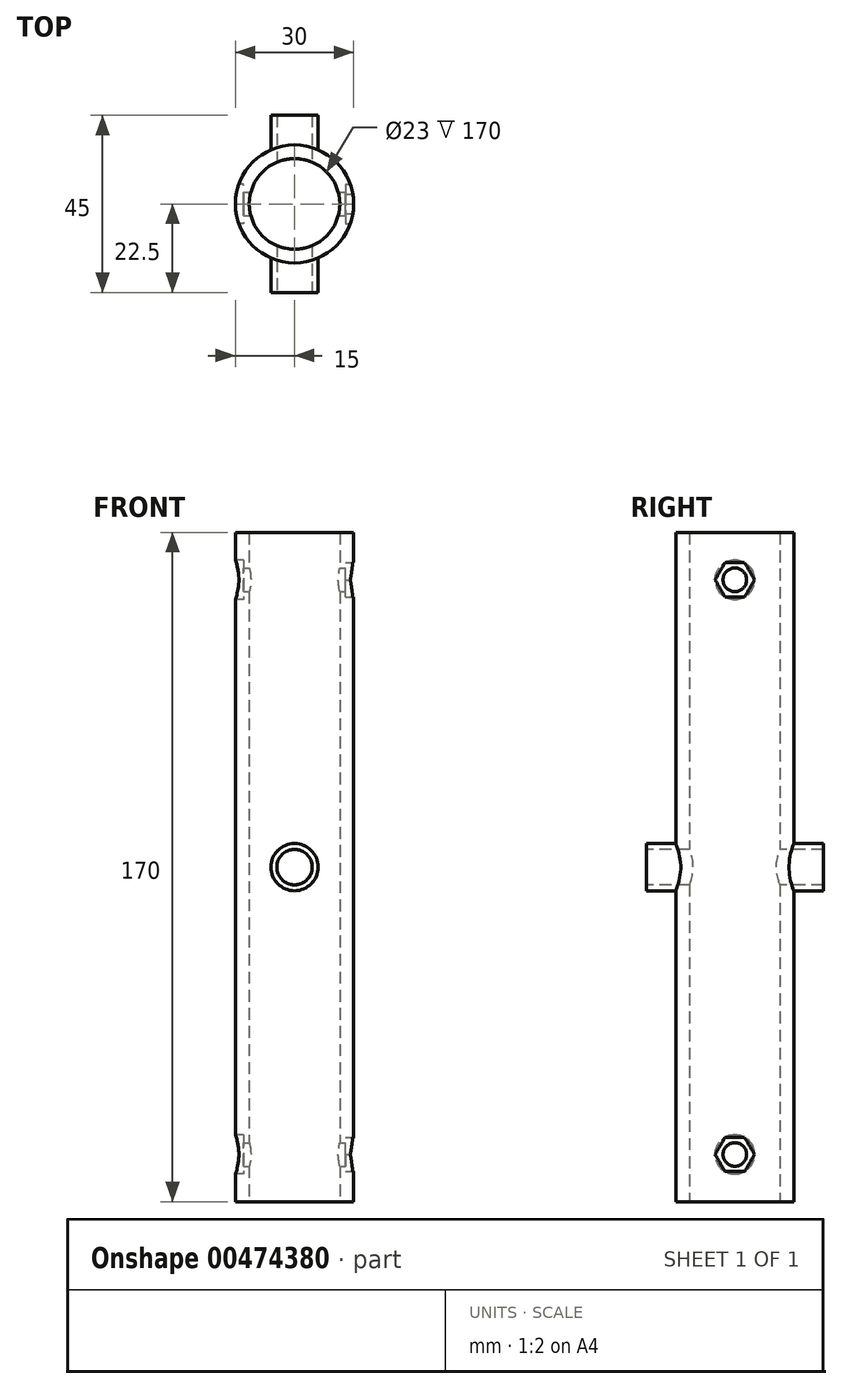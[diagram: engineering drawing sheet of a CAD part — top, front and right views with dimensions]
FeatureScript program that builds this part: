
annotation { "Feature Type Name" : "Feature", "Feature Type Description" : "" }
export const myFeature = defineFeature(function(context is Context, id is Id, definition is map)
    precondition{}
    {
        {
            var Q0;
            Q0=qCreatedBy(makeId("Top.planeOp"),FACE);
            var sketch = newSketch(context, id + "F0", { "sketchPlane" : qUnion([Q0])});
            skCircle(sketch, "E0", {"center": v(0, 0) * mm, "radius": 15 * mm});
            skCircle(sketch, "E1", {"center": v(0, 0) * mm, "radius": 11.5 * mm});
            skSolve(sketch);
        }
        {
            var Q0;
            Q0=makeQuery(id+"F0.imprint","IMPRINT",FACE,{"disambiguationData":[TD([[makeQuery(id+"F0.imprint","IMPRINT",EDGE,{"derivedFrom":sQuery(id+"F0.wireOp",EDGE,"E0")}),1.0]])]});
            extrude(context, id + "F1", {"entities" : qUnion([Q0]), "depth" : 170 * mm});
        }
        {
            var Q0;
            Q0=qCreatedBy(makeId("Front.planeOp"),FACE);
            var sketch = newSketch(context, id + "F2", { "sketchPlane" : qUnion([Q0])});
            skCircle(sketch, "E2", {"center": v(0, 85) * mm, "radius": 4.5 * mm});
            skSolve(sketch);
        }
        {
            var Q0;
            Q0 = qSketchRegion(id + "F2", true);
            extrude(context, id + "F3", {"entities" : qUnion([Q0]), "operationType" : NewBodyOperationType.REMOVE, "endBound" : BoundingType.THROUGH_ALL, "oppositeDirection" : true, "depth" : 25 * mm, "hasSecondDirection" : true, "secondDirectionBound" : SecondDirectionBoundingType.THROUGH_ALL, "secondDirectionOppositeDirection" : false, "secondDirectionDepth" : 25 * mm});
        }
        {
            var Q0;
            Q0=qCreatedBy(makeId("Front.planeOp"),FACE);
            cPlane(context, id + "F4", {"entities" : qUnion([Q0]), "cplaneType" : CPlaneType.OFFSET, "offset" : 17.5 * mm, "width" : 150 * mm, "height" : 150 * mm});
        }
        {
            var Q0;
            Q0=qCreatedBy(id+"F4.planeOp",FACE);
            var sketch = newSketch(context, id + "F5", { "sketchPlane" : qUnion([Q0])});
            skCircle(sketch, "E3", {"center": v(0, 85) * mm, "radius": 6 * mm});
            skCircle(sketch, "E4.0", {"center": v(0, 85) * mm, "radius": 4.5 * mm});
            skSolve(sketch);
        }
        {
            var Q0;
            Q0 = qSketchRegion(id + "F5", true);
            var Q1;
            Q1=makeQuery(id+"F1.opExtrude","SWEPT_FACE",FACE,{"disambiguationData":[OSD([sQuery(id+"F0.wireOp",EDGE,"E0")])]});
            extrude(context, id + "F6", {"entities" : qUnion([Q0]), "operationType" : NewBodyOperationType.ADD, "depth" : 5 * mm, "hasSecondDirection" : true, "secondDirectionBound" : SecondDirectionBoundingType.UP_TO_SURFACE, "secondDirectionOppositeDirection" : true, "secondDirectionBoundEntityFace" : qUnion([Q1]), "secondDirectionDepth" : 25 * mm});
        }
        {
            var Q0;
            Q0=qCreatedBy(makeId("Front.planeOp"),FACE);
            cPlane(context, id + "F7", {"entities" : qUnion([Q0]), "cplaneType" : CPlaneType.OFFSET, "offset" : 17.5 * mm, "oppositeDirection" : true, "width" : 150 * mm, "height" : 150 * mm});
        }
        {
            var Q0;
            Q0=qCreatedBy(id+"F7.planeOp",FACE);
            var sketch = newSketch(context, id + "F8", { "sketchPlane" : qUnion([Q0])});
            skCircle(sketch, "E5.0", {"center": v(0, 85) * mm, "radius": 6 * mm});
            skCircle(sketch, "E6.0", {"center": v(0, 85) * mm, "radius": 4.5 * mm});
            skSolve(sketch);
        }
        {
            var Q0;
            Q0=makeQuery(id+"F8.imprint","IMPRINT",FACE,{"disambiguationData":[TD([[makeQuery(id+"F8.imprint","IMPRINT",EDGE,{"derivedFrom":sQuery(id+"F8.wireOp",EDGE,"E5.0")}),1.0]])]});
            var Q1;
            Q1=makeQuery(id+"F1.opExtrude","SWEPT_FACE",FACE,{"disambiguationData":[OSD([sQuery(id+"F0.wireOp",EDGE,"E0")])]});
            extrude(context, id + "F9", {"entities" : qUnion([Q0]), "operationType" : NewBodyOperationType.ADD, "oppositeDirection" : true, "depth" : 5 * mm, "hasSecondDirection" : true, "secondDirectionBound" : SecondDirectionBoundingType.UP_TO_SURFACE, "secondDirectionOppositeDirection" : false, "secondDirectionBoundEntityFace" : qUnion([Q1]), "secondDirectionDepth" : 2 * mm});
        }
        {
            var Q0;
            Q0=qCreatedBy(makeId("Right.planeOp"),FACE);
            var sketch = newSketch(context, id + "F10", { "sketchPlane" : qUnion([Q0])});
            skCircle(sketch, "E7", {"center": v(0, 12) * mm, "radius": 3 * mm});
            skCircle(sketch, "E8", {"center": v(0, 158) * mm, "radius": 3 * mm});
            skLineSegment(sketch, "E9.0", {"start": v(-15, 170) * mm, "end": v(15, 170) * mm, "construction": true});
            skLineSegment(sketch, "E10", {"start": v(-15, 0) * mm, "end": v(-15, 100) * mm, "construction": true});
            skLineSegment(sketch, "E11", {"start": v(15, 100) * mm, "end": v(15, 0) * mm, "construction": true});
            skSolve(sketch);
        }
        {
            var Q0;
            Q0 = qSketchRegion(id + "F10", true);
            extrude(context, id + "F11", {"entities" : qUnion([Q0]), "operationType" : NewBodyOperationType.REMOVE, "endBound" : BoundingType.THROUGH_ALL, "oppositeDirection" : true, "depth" : 25 * mm, "hasSecondDirection" : true, "secondDirectionBound" : SecondDirectionBoundingType.THROUGH_ALL, "secondDirectionOppositeDirection" : false, "secondDirectionDepth" : 25 * mm});
        }
        {
            var Q0;
            Q0=qCreatedBy(makeId("Right.planeOp"),FACE);
            cPlane(context, id + "F12", {"entities" : qUnion([Q0]), "cplaneType" : CPlaneType.OFFSET, "offset" : 15 * mm, "width" : 150 * mm, "height" : 150 * mm});
        }
        {
            var Q0;
            Q0=qCreatedBy(id+"F12.planeOp",FACE);
            var sketch = newSketch(context, id + "F13", { "sketchPlane" : qUnion([Q0])});
            skCircle(sketch, "E12.0", {"center": v(0, 158) * mm, "radius": 3 * mm, "construction": true});
            skLineSegment(sketch, "E13", {"start": v(-5, 158) * mm, "end": v(-2.5, 162.33) * mm});
            skLineSegment(sketch, "E14", {"start": v(-2.5, 162.33) * mm, "end": v(2.5, 162.33) * mm});
            skLineSegment(sketch, "E15", {"start": v(2.5, 162.33) * mm, "end": v(5, 158) * mm});
            skLineSegment(sketch, "E16", {"start": v(5, 158) * mm, "end": v(2.5, 153.67) * mm});
            skLineSegment(sketch, "E17", {"start": v(2.5, 153.67) * mm, "end": v(-2.5, 153.67) * mm});
            skLineSegment(sketch, "E18", {"start": v(-2.5, 153.67) * mm, "end": v(-5, 158) * mm});
            skLineSegment(sketch, "E19", {"start": v(-23.18, 85) * mm, "end": v(26.08, 85) * mm, "construction": true});
            skLineSegment(sketch, "E20.MirrorCS", {"start": v(2.5, 16.33) * mm, "end": v(-2.5, 16.33) * mm});
            skLineSegment(sketch, "E21.MirrorCS", {"start": v(5, 12) * mm, "end": v(2.5, 16.33) * mm});
            skLineSegment(sketch, "E22.MirrorCS", {"start": v(2.5, 7.67) * mm, "end": v(5, 12) * mm});
            skLineSegment(sketch, "E23.MirrorCS", {"start": v(-2.5, 16.33) * mm, "end": v(-5, 12) * mm});
            skLineSegment(sketch, "E24.MirrorCS", {"start": v(-5, 12) * mm, "end": v(-2.5, 7.67) * mm});
            skLineSegment(sketch, "E25.MirrorCS", {"start": v(-2.5, 7.67) * mm, "end": v(2.5, 7.67) * mm});
            skLineSegment(sketch, "E26.0", {"start": v(-15, 170) * mm, "end": v(15, 170) * mm, "construction": true});
            skSolve(sketch);
        }
        {
            var Q0;
            Q0 = qSketchRegion(id + "F13", true);
            extrude(context, id + "F14", {"entities" : qUnion([Q0]), "operationType" : NewBodyOperationType.REMOVE, "oppositeDirection" : true, "depth" : 2 * mm});
        }
        {
            var Q0;
            Q0=qCreatedBy(makeId("Right.planeOp"),FACE);
            cPlane(context, id + "F15", {"entities" : qUnion([Q0]), "cplaneType" : CPlaneType.OFFSET, "offset" : 15 * mm, "oppositeDirection" : true, "width" : 150 * mm, "height" : 150 * mm});
        }
        {
            var Q0;
            Q0=qCreatedBy(id+"F15.planeOp",FACE);
            var sketch = newSketch(context, id + "F16", { "sketchPlane" : qUnion([Q0])});
            skCircle(sketch, "E27.0", {"center": v(0, 158) * mm, "radius": 3 * mm, "construction": true});
            skCircle(sketch, "E28.0", {"center": v(0, 12) * mm, "radius": 3 * mm, "construction": true});
            skCircle(sketch, "E29", {"center": v(0, 158) * mm, "radius": 5 * mm});
            skCircle(sketch, "E30", {"center": v(0, 12) * mm, "radius": 5 * mm});
            skSolve(sketch);
        }
        {
            var Q0;
            Q0 = qSketchRegion(id + "F16", true);
            extrude(context, id + "F17", {"entities" : qUnion([Q0]), "operationType" : NewBodyOperationType.REMOVE, "depth" : 2 * mm});
        }
    });
